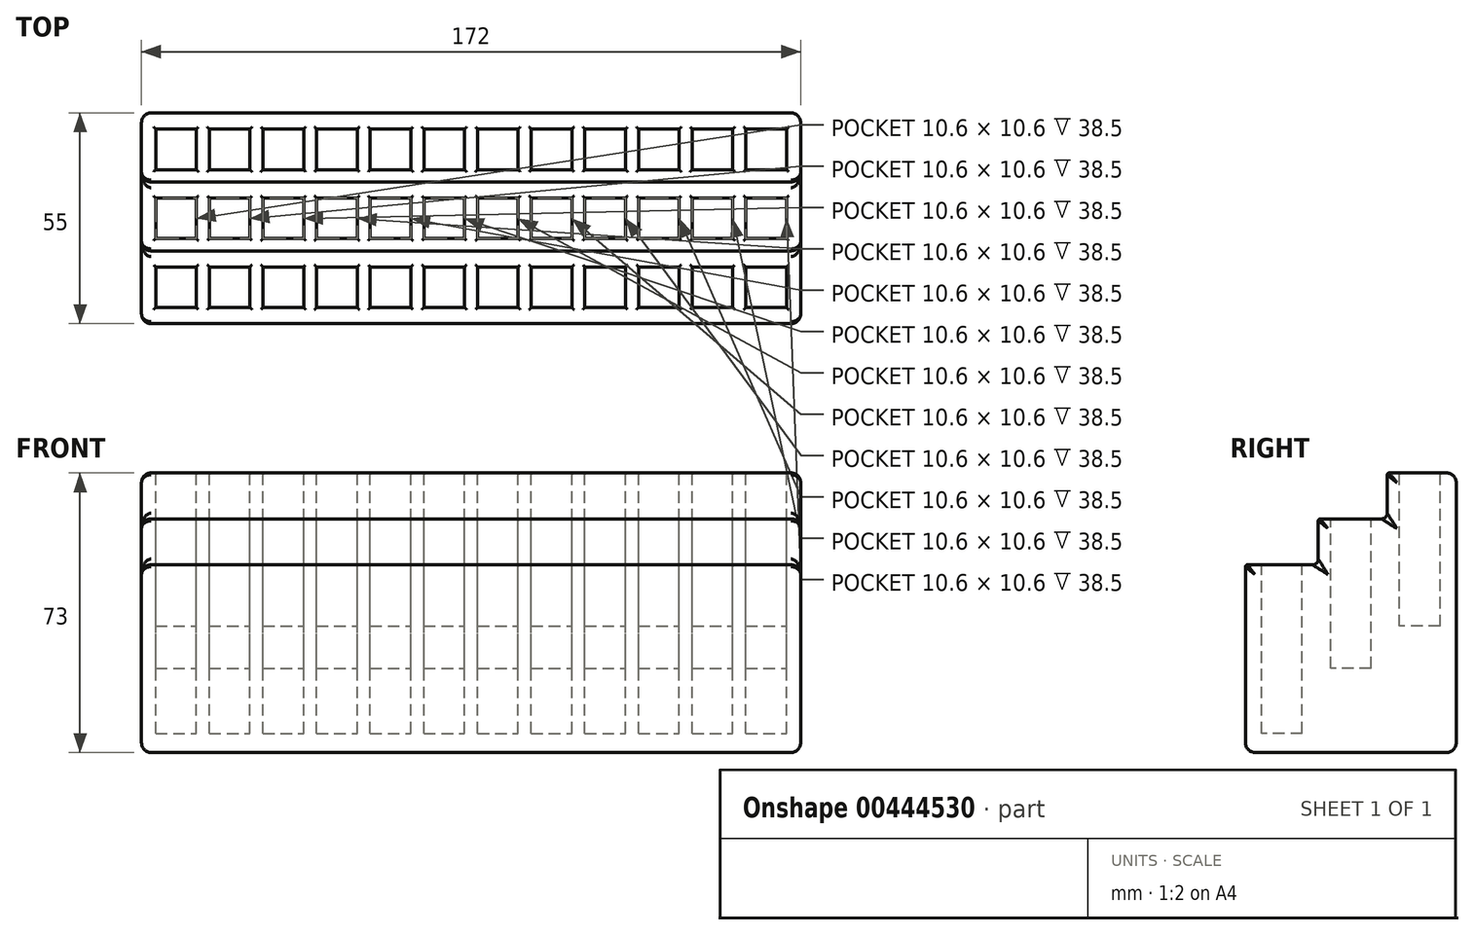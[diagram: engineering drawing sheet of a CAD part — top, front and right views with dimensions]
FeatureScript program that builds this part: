
annotation { "Feature Type Name" : "Feature", "Feature Type Description" : "" }
export const myFeature = defineFeature(function(context is Context, id is Id, definition is map)
    precondition{}
    {
        {
            var Q0;
            Q0=qCreatedBy(makeId("Top.planeOp"),FACE);
            var sketch = newSketch(context, id + "F0", { "sketchPlane" : qUnion([Q0])});
            skLineSegment(sketch, "E0.bottom", {"start": v(-55.78, 92.87) * mm, "end": v(116.22, 92.87) * mm});
            skLineSegment(sketch, "E0.top", {"start": v(-55.78, 37.87) * mm, "end": v(116.22, 37.87) * mm});
            skLineSegment(sketch, "E0.left", {"start": v(-55.78, 92.87) * mm, "end": v(-55.78, 37.87) * mm});
            skLineSegment(sketch, "E0.right", {"start": v(116.22, 92.87) * mm, "end": v(116.22, 37.87) * mm});
            skSolve(sketch);
        }
        {
            var Q0;
            Q0=makeQuery(id+"F0.imprint","IMPRINT",FACE,{"disambiguationData":[TD([[makeQuery(id+"F0.imprint","IMPRINT",EDGE,{"derivedFrom":sQuery(id+"F0.wireOp",EDGE,"2cde3dd9-bf48-4d98-be25-aab0bfc94084.7.2.0")}),-1.0]])]});
            var Q1;
            Q1=makeQuery(id+"F0.imprint","IMPRINT",FACE,{"disambiguationData":[TD([[makeQuery(id+"F0.imprint","IMPRINT",EDGE,{"derivedFrom":sQuery(id+"F0.wireOp",EDGE,"2cde3dd9-bf48-4d98-be25-aab0bfc94084.4.0.0")}),-1.0]])]});
            var Q2;
            Q2=makeQuery(id+"F0.imprint","IMPRINT",FACE,{"disambiguationData":[TD([[makeQuery(id+"F0.imprint","IMPRINT",EDGE,{"derivedFrom":sQuery(id+"F0.wireOp",EDGE,"2cde3dd9-bf48-4d98-be25-aab0bfc94084.3.0.0")}),-1.0]])]});
            var Q3;
            Q3=makeQuery(id+"F0.imprint","IMPRINT",FACE,{"disambiguationData":[TD([[makeQuery(id+"F0.imprint","IMPRINT",EDGE,{"derivedFrom":sQuery(id+"F0.wireOp",EDGE,"2cde3dd9-bf48-4d98-be25-aab0bfc94084.9.2.0")}),-1.0]])]});
            var Q4;
            Q4=makeQuery(id+"F0.imprint","IMPRINT",FACE,{"disambiguationData":[TD([[makeQuery(id+"F0.imprint","IMPRINT",EDGE,{"derivedFrom":sQuery(id+"F0.wireOp",EDGE,"2cde3dd9-bf48-4d98-be25-aab0bfc94084.7.1.0")}),-1.0]])]});
            var Q5;
            Q5=makeQuery(id+"F0.imprint","IMPRINT",FACE,{"disambiguationData":[TD([[makeQuery(id+"F0.imprint","IMPRINT",EDGE,{"derivedFrom":sQuery(id+"F0.wireOp",EDGE,"2cde3dd9-bf48-4d98-be25-aab0bfc94084.0.1.0")}),1.0]])]});
            var Q6;
            Q6=makeQuery(id+"F0.imprint","IMPRINT",FACE,{"disambiguationData":[TD([[makeQuery(id+"F0.imprint","IMPRINT",EDGE,{"derivedFrom":sQuery(id+"F0.wireOp",EDGE,"2cde3dd9-bf48-4d98-be25-aab0bfc94084.8.1.0")}),-1.0]])]});
            var Q7;
            {var subQ0=sQuery(id+"F0.wireOp",EDGE,"E0.top");Q7=makeQuery(id+"F0.imprint","IMPRINT",FACE,{"disambiguationData":[TD([[makeQuery(id+"F0.imprint","IMPRINT",EDGE,{"derivedFrom":subQ0}),1.0]])]});}
            var Q8;
            Q8=makeQuery(id+"F0.imprint","IMPRINT",FACE,{"disambiguationData":[TD([[makeQuery(id+"F0.imprint","IMPRINT",EDGE,{"derivedFrom":sQuery(id+"F0.wireOp",EDGE,"2cde3dd9-bf48-4d98-be25-aab0bfc94084.11.2.0")}),-1.0]])]});
            var Q9;
            Q9=makeQuery(id+"F0.imprint","IMPRINT",FACE,{"disambiguationData":[TD([[makeQuery(id+"F0.imprint","IMPRINT",EDGE,{"derivedFrom":sQuery(id+"F0.wireOp",EDGE,"2cde3dd9-bf48-4d98-be25-aab0bfc94084.5.1.0")}),-1.0]])]});
            var Q10;
            Q10=makeQuery(id+"F0.imprint","IMPRINT",FACE,{"disambiguationData":[TD([[makeQuery(id+"F0.imprint","IMPRINT",EDGE,{"derivedFrom":sQuery(id+"F0.wireOp",EDGE,"2cde3dd9-bf48-4d98-be25-aab0bfc94084.11.1.0")}),-1.0]])]});
            var Q11;
            Q11=makeQuery(id+"F0.imprint","IMPRINT",FACE,{"disambiguationData":[TD([[makeQuery(id+"F0.imprint","IMPRINT",EDGE,{"derivedFrom":sQuery(id+"F0.wireOp",EDGE,"2cde3dd9-bf48-4d98-be25-aab0bfc94084.11.0.0")}),-1.0]])]});
            var Q12;
            Q12=makeQuery(id+"F0.imprint","IMPRINT",FACE,{"disambiguationData":[TD([[makeQuery(id+"F0.imprint","IMPRINT",EDGE,{"derivedFrom":sQuery(id+"F0.wireOp",EDGE,"2cde3dd9-bf48-4d98-be25-aab0bfc94084.5.0.0")}),-1.0]])]});
            var Q13;
            Q13=makeQuery(id+"F0.imprint","IMPRINT",FACE,{"disambiguationData":[TD([[makeQuery(id+"F0.imprint","IMPRINT",EDGE,{"derivedFrom":sQuery(id+"F0.wireOp",EDGE,"2cde3dd9-bf48-4d98-be25-aab0bfc94084.7.0.0")}),-1.0]])]});
            var Q14;
            Q14=makeQuery(id+"F0.imprint","IMPRINT",FACE,{"disambiguationData":[TD([[makeQuery(id+"F0.imprint","IMPRINT",EDGE,{"derivedFrom":sQuery(id+"F0.wireOp",EDGE,"2cde3dd9-bf48-4d98-be25-aab0bfc94084.6.2.0")}),-1.0]])]});
            var Q15;
            {var subQ1=sQuery(id+"F0.wireOp",EDGE,"E0.bottom");Q15=makeQuery(id+"F0.imprint","IMPRINT",FACE,{"disambiguationData":[TD([[makeQuery(id+"F0.imprint","IMPRINT",EDGE,{"derivedFrom":subQ1}),-1.0]])]});}
            var Q16;
            Q16=makeQuery(id+"F0.imprint","IMPRINT",FACE,{"disambiguationData":[TD([[makeQuery(id+"F0.imprint","IMPRINT",EDGE,{"derivedFrom":sQuery(id+"F0.wireOp",EDGE,"2cde3dd9-bf48-4d98-be25-aab0bfc94084.10.0.0")}),-1.0]])]});
            var Q17;
            Q17=makeQuery(id+"F0.imprint","IMPRINT",FACE,{"disambiguationData":[TD([[makeQuery(id+"F0.imprint","IMPRINT",EDGE,{"derivedFrom":sQuery(id+"F0.wireOp",EDGE,"2cde3dd9-bf48-4d98-be25-aab0bfc94084.6.1.0")}),-1.0]])]});
            var Q18;
            Q18=makeQuery(id+"F0.imprint","IMPRINT",FACE,{"disambiguationData":[TD([[makeQuery(id+"F0.imprint","IMPRINT",EDGE,{"derivedFrom":sQuery(id+"F0.wireOp",EDGE,"2cde3dd9-bf48-4d98-be25-aab0bfc94084.6.0.0")}),-1.0]])]});
            var Q19;
            Q19=makeQuery(id+"F0.imprint","IMPRINT",FACE,{"disambiguationData":[TD([[makeQuery(id+"F0.imprint","IMPRINT",EDGE,{"derivedFrom":sQuery(id+"F0.wireOp",EDGE,"2cde3dd9-bf48-4d98-be25-aab0bfc94084.9.1.0")}),-1.0]])]});
            var Q20;
            Q20=makeQuery(id+"F0.imprint","IMPRINT",FACE,{"disambiguationData":[TD([[makeQuery(id+"F0.imprint","IMPRINT",EDGE,{"derivedFrom":sQuery(id+"F0.wireOp",EDGE,"2cde3dd9-bf48-4d98-be25-aab0bfc94084.9.0.0")}),-1.0]])]});
            var Q21;
            Q21=makeQuery(id+"F0.imprint","IMPRINT",FACE,{"disambiguationData":[TD([[makeQuery(id+"F0.imprint","IMPRINT",EDGE,{"derivedFrom":sQuery(id+"F0.wireOp",EDGE,"2cde3dd9-bf48-4d98-be25-aab0bfc94084.8.0.0")}),-1.0]])]});
            var Q22;
            Q22=makeQuery(id+"F0.imprint","IMPRINT",FACE,{"disambiguationData":[TD([[makeQuery(id+"F0.imprint","IMPRINT",EDGE,{"derivedFrom":sQuery(id+"F0.wireOp",EDGE,"2cde3dd9-bf48-4d98-be25-aab0bfc94084.10.1.0")}),-1.0]])]});
            var Q23;
            Q23=makeQuery(id+"F0.imprint","IMPRINT",FACE,{"disambiguationData":[TD([[makeQuery(id+"F0.imprint","IMPRINT",EDGE,{"derivedFrom":sQuery(id+"F0.wireOp",EDGE,"2cde3dd9-bf48-4d98-be25-aab0bfc94084.10.2.0")}),-1.0]])]});
            var Q24;
            Q24=makeQuery(id+"F0.imprint","IMPRINT",FACE,{"disambiguationData":[TD([[makeQuery(id+"F0.imprint","IMPRINT",EDGE,{"derivedFrom":sQuery(id+"F0.wireOp",EDGE,"2cde3dd9-bf48-4d98-be25-aab0bfc94084.8.2.0")}),-1.0]])]});
            var Q25;
            Q25=makeQuery(id+"F0.imprint","IMPRINT",FACE,{"disambiguationData":[TD([[makeQuery(id+"F0.imprint","IMPRINT",EDGE,{"derivedFrom":sQuery(id+"F0.wireOp",EDGE,"2cde3dd9-bf48-4d98-be25-aab0bfc94084.3.2.0")}),-1.0]])]});
            var Q26;
            Q26=makeQuery(id+"F0.imprint","IMPRINT",FACE,{"disambiguationData":[TD([[makeQuery(id+"F0.imprint","IMPRINT",EDGE,{"derivedFrom":sQuery(id+"F0.wireOp",EDGE,"2cde3dd9-bf48-4d98-be25-aab0bfc94084.3.1.0")}),-1.0]])]});
            var Q27;
            Q27=makeQuery(id+"F0.imprint","IMPRINT",FACE,{"disambiguationData":[TD([[makeQuery(id+"F0.imprint","IMPRINT",EDGE,{"derivedFrom":sQuery(id+"F0.wireOp",EDGE,"2cde3dd9-bf48-4d98-be25-aab0bfc94084.2.2.0")}),-1.0]])]});
            var Q28;
            Q28=makeQuery(id+"F0.imprint","IMPRINT",FACE,{"disambiguationData":[TD([[makeQuery(id+"F0.imprint","IMPRINT",EDGE,{"derivedFrom":sQuery(id+"F0.wireOp",EDGE,"2cde3dd9-bf48-4d98-be25-aab0bfc94084.2.1.0")}),-1.0]])]});
            var Q29;
            Q29=makeQuery(id+"F0.imprint","IMPRINT",FACE,{"disambiguationData":[TD([[makeQuery(id+"F0.imprint","IMPRINT",EDGE,{"derivedFrom":sQuery(id+"F0.wireOp",EDGE,"2cde3dd9-bf48-4d98-be25-aab0bfc94084.0.2.0")}),-1.0]])]});
            var Q30;
            Q30=makeQuery(id+"F0.imprint","IMPRINT",FACE,{"disambiguationData":[TD([[makeQuery(id+"F0.imprint","IMPRINT",EDGE,{"derivedFrom":sQuery(id+"F0.wireOp",EDGE,"2cde3dd9-bf48-4d98-be25-aab0bfc94084.2.0.0")}),-1.0]])]});
            var Q31;
            Q31=makeQuery(id+"F0.imprint","IMPRINT",FACE,{"disambiguationData":[TD([[makeQuery(id+"F0.imprint","IMPRINT",EDGE,{"derivedFrom":sQuery(id+"F0.wireOp",EDGE,"2cde3dd9-bf48-4d98-be25-aab0bfc94084.1.2.0")}),-1.0]])]});
            var Q32;
            Q32=makeQuery(id+"F0.imprint","IMPRINT",FACE,{"disambiguationData":[TD([[makeQuery(id+"F0.imprint","IMPRINT",EDGE,{"derivedFrom":sQuery(id+"F0.wireOp",EDGE,"2cde3dd9-bf48-4d98-be25-aab0bfc94084.1.0.0")}),-1.0]])]});
            var Q33;
            Q33=makeQuery(id+"F0.imprint","IMPRINT",FACE,{"disambiguationData":[TD([[makeQuery(id+"F0.imprint","IMPRINT",EDGE,{"derivedFrom":sQuery(id+"F0.wireOp",EDGE,"2cde3dd9-bf48-4d98-be25-aab0bfc94084.0.1.0")}),-1.0]])]});
            var Q34;
            Q34=makeQuery(id+"F0.imprint","IMPRINT",FACE,{"disambiguationData":[TD([[makeQuery(id+"F0.imprint","IMPRINT",EDGE,{"derivedFrom":sQuery(id+"F0.wireOp",EDGE,"2cde3dd9-bf48-4d98-be25-aab0bfc94084.5.2.0")}),-1.0]])]});
            var Q35;
            Q35=makeQuery(id+"F0.imprint","IMPRINT",FACE,{"disambiguationData":[TD([[makeQuery(id+"F0.imprint","IMPRINT",EDGE,{"derivedFrom":sQuery(id+"F0.wireOp",EDGE,"2cde3dd9-bf48-4d98-be25-aab0bfc94084.1.1.0")}),-1.0]])]});
            var Q36;
            Q36=makeQuery(id+"F0.imprint","IMPRINT",FACE,{"disambiguationData":[TD([[makeQuery(id+"F0.imprint","IMPRINT",EDGE,{"derivedFrom":sQuery(id+"F0.wireOp",EDGE,"2cde3dd9-bf48-4d98-be25-aab0bfc94084.4.1.0")}),-1.0]])]});
            var Q37;
            Q37=makeQuery(id+"F0.imprint","IMPRINT",FACE,{"disambiguationData":[TD([[makeQuery(id+"F0.imprint","IMPRINT",EDGE,{"derivedFrom":sQuery(id+"F0.wireOp",EDGE,"2cde3dd9-bf48-4d98-be25-aab0bfc94084.4.2.0")}),-1.0]])]});
            var Q38;
            Q38=makeQuery(id+"F0.imprint","IMPRINT",FACE,{"disambiguationData":[TD([[makeQuery(id+"F0.imprint","IMPRINT",EDGE,{"derivedFrom":sQuery(id+"F0.wireOp",EDGE,"MJ5tnMIe-62KD-FdFw-GlkB-I08ag2kGYmXd.bottom")}),-1.0]])]});
            extrude(context, id + "F1", {"entities" : qUnion([Q0, Q1, Q2, Q3, Q4, Q5, Q6, Q7, Q8, Q9, Q10, Q11, Q12, Q13, Q14, Q15, Q16, Q17, Q18, Q19, Q20, Q21, Q22, Q23, Q24, Q25, Q26, Q27, Q28, Q29, Q30, Q31, Q32, Q33, Q34, Q35, Q36, Q37, Q38]), "oppositeDirection" : true, "depth" : 73 * mm});
        }
        {
            var Q0;
            Q0=makeQuery(id+"F1.opExtrude","CAP_FACE",FACE,{"disambiguationData":[OSD([sQuery(id+"F0.wireOp",EDGE,"E0.bottom"),sQuery(id+"F0.wireOp",EDGE,"E0.top"),sQuery(id+"F0.wireOp",EDGE,"E0.left"),sQuery(id+"F0.wireOp",EDGE,"E0.right")])],"isStart":true});
            var sketch = newSketch(context, id + "F2", { "sketchPlane" : qUnion([Q0])});
            skLineSegment(sketch, "E1.0", {"start": v(-55.78, 37.87) * mm, "end": v(116.22, 37.87) * mm});
            skLineSegment(sketch, "E2.0", {"start": v(116.22, 92.87) * mm, "end": v(116.22, 37.87) * mm});
            skLineSegment(sketch, "E3.0", {"start": v(-55.78, 92.87) * mm, "end": v(116.22, 92.87) * mm});
            skLineSegment(sketch, "E4.0", {"start": v(-55.78, 92.87) * mm, "end": v(-55.78, 37.87) * mm});
            skLineSegment(sketch, "E5.bottom", {"start": v(-52.08, 88.67) * mm, "end": v(-41.48, 88.67) * mm});
            skLineSegment(sketch, "E5.top", {"start": v(-52.08, 78.07) * mm, "end": v(-41.48, 78.07) * mm});
            skLineSegment(sketch, "E5.left", {"start": v(-52.08, 88.67) * mm, "end": v(-52.08, 78.07) * mm});
            skLineSegment(sketch, "E5.right", {"start": v(-41.48, 88.67) * mm, "end": v(-41.48, 78.07) * mm});
            skLineSegment(sketch, "E6.0.1.0", {"start": v(-52.08, 60.07) * mm, "end": v(-41.48, 60.07) * mm});
            skLineSegment(sketch, "E6.0.1.1", {"start": v(-41.48, 70.67) * mm, "end": v(-41.48, 60.07) * mm});
            skLineSegment(sketch, "E6.0.1.2", {"start": v(-52.08, 70.67) * mm, "end": v(-52.08, 60.07) * mm});
            skLineSegment(sketch, "E6.0.1.3", {"start": v(-52.08, 70.67) * mm, "end": v(-41.48, 70.67) * mm});
            skLineSegment(sketch, "E6.0.2.0", {"start": v(-52.08, 42.07) * mm, "end": v(-41.48, 42.07) * mm});
            skLineSegment(sketch, "E6.0.2.1", {"start": v(-41.48, 52.67) * mm, "end": v(-41.48, 42.07) * mm});
            skLineSegment(sketch, "E6.0.2.2", {"start": v(-52.08, 52.67) * mm, "end": v(-52.08, 42.07) * mm});
            skLineSegment(sketch, "E6.0.2.3", {"start": v(-52.08, 52.67) * mm, "end": v(-41.48, 52.67) * mm});
            skLineSegment(sketch, "E6.1.0.0", {"start": v(-38.08, 78.07) * mm, "end": v(-27.48, 78.07) * mm});
            skLineSegment(sketch, "E6.1.0.1", {"start": v(-27.48, 88.67) * mm, "end": v(-27.48, 78.07) * mm});
            skLineSegment(sketch, "E6.1.0.2", {"start": v(-38.08, 88.67) * mm, "end": v(-38.08, 78.07) * mm});
            skLineSegment(sketch, "E6.1.0.3", {"start": v(-38.08, 88.67) * mm, "end": v(-27.48, 88.67) * mm});
            skLineSegment(sketch, "E6.1.1.0", {"start": v(-38.08, 60.07) * mm, "end": v(-27.48, 60.07) * mm});
            skLineSegment(sketch, "E6.1.1.1", {"start": v(-27.48, 70.67) * mm, "end": v(-27.48, 60.07) * mm});
            skLineSegment(sketch, "E6.1.1.2", {"start": v(-38.08, 70.67) * mm, "end": v(-38.08, 60.07) * mm});
            skLineSegment(sketch, "E6.1.1.3", {"start": v(-38.08, 70.67) * mm, "end": v(-27.48, 70.67) * mm});
            skLineSegment(sketch, "E6.1.2.0", {"start": v(-38.08, 42.07) * mm, "end": v(-27.48, 42.07) * mm});
            skLineSegment(sketch, "E6.1.2.1", {"start": v(-27.48, 52.67) * mm, "end": v(-27.48, 42.07) * mm});
            skLineSegment(sketch, "E6.1.2.2", {"start": v(-38.08, 52.67) * mm, "end": v(-38.08, 42.07) * mm});
            skLineSegment(sketch, "E6.1.2.3", {"start": v(-38.08, 52.67) * mm, "end": v(-27.48, 52.67) * mm});
            skLineSegment(sketch, "E6.2.0.0", {"start": v(-24.08, 78.07) * mm, "end": v(-13.48, 78.07) * mm});
            skLineSegment(sketch, "E6.2.0.1", {"start": v(-13.48, 88.67) * mm, "end": v(-13.48, 78.07) * mm});
            skLineSegment(sketch, "E6.2.0.2", {"start": v(-24.08, 88.67) * mm, "end": v(-24.08, 78.07) * mm});
            skLineSegment(sketch, "E6.2.0.3", {"start": v(-24.08, 88.67) * mm, "end": v(-13.48, 88.67) * mm});
            skLineSegment(sketch, "E6.2.1.0", {"start": v(-24.08, 60.07) * mm, "end": v(-13.48, 60.07) * mm});
            skLineSegment(sketch, "E6.2.1.1", {"start": v(-13.48, 70.67) * mm, "end": v(-13.48, 60.07) * mm});
            skLineSegment(sketch, "E6.2.1.2", {"start": v(-24.08, 70.67) * mm, "end": v(-24.08, 60.07) * mm});
            skLineSegment(sketch, "E6.2.1.3", {"start": v(-24.08, 70.67) * mm, "end": v(-13.48, 70.67) * mm});
            skLineSegment(sketch, "E6.2.2.0", {"start": v(-24.08, 42.07) * mm, "end": v(-13.48, 42.07) * mm});
            skLineSegment(sketch, "E6.2.2.1", {"start": v(-13.48, 52.67) * mm, "end": v(-13.48, 42.07) * mm});
            skLineSegment(sketch, "E6.2.2.2", {"start": v(-24.08, 52.67) * mm, "end": v(-24.08, 42.07) * mm});
            skLineSegment(sketch, "E6.2.2.3", {"start": v(-24.08, 52.67) * mm, "end": v(-13.48, 52.67) * mm});
            skLineSegment(sketch, "E6.3.0.0", {"start": v(-10.08, 78.07) * mm, "end": v(0.52, 78.07) * mm});
            skLineSegment(sketch, "E6.3.0.1", {"start": v(0.52, 88.67) * mm, "end": v(0.52, 78.07) * mm});
            skLineSegment(sketch, "E6.3.0.2", {"start": v(-10.08, 88.67) * mm, "end": v(-10.08, 78.07) * mm});
            skLineSegment(sketch, "E6.3.0.3", {"start": v(-10.08, 88.67) * mm, "end": v(0.52, 88.67) * mm});
            skLineSegment(sketch, "E6.3.1.0", {"start": v(-10.08, 60.07) * mm, "end": v(0.52, 60.07) * mm});
            skLineSegment(sketch, "E6.3.1.1", {"start": v(0.52, 70.67) * mm, "end": v(0.52, 60.07) * mm});
            skLineSegment(sketch, "E6.3.1.2", {"start": v(-10.08, 70.67) * mm, "end": v(-10.08, 60.07) * mm});
            skLineSegment(sketch, "E6.3.1.3", {"start": v(-10.08, 70.67) * mm, "end": v(0.52, 70.67) * mm});
            skLineSegment(sketch, "E6.3.2.0", {"start": v(-10.08, 42.07) * mm, "end": v(0.52, 42.07) * mm});
            skLineSegment(sketch, "E6.3.2.1", {"start": v(0.52, 52.67) * mm, "end": v(0.52, 42.07) * mm});
            skLineSegment(sketch, "E6.3.2.2", {"start": v(-10.08, 52.67) * mm, "end": v(-10.08, 42.07) * mm});
            skLineSegment(sketch, "E6.3.2.3", {"start": v(-10.08, 52.67) * mm, "end": v(0.52, 52.67) * mm});
            skLineSegment(sketch, "E6.4.0.0", {"start": v(3.92, 78.07) * mm, "end": v(14.52, 78.07) * mm});
            skLineSegment(sketch, "E6.4.0.1", {"start": v(14.52, 88.67) * mm, "end": v(14.52, 78.07) * mm});
            skLineSegment(sketch, "E6.4.0.2", {"start": v(3.92, 88.67) * mm, "end": v(3.92, 78.07) * mm});
            skLineSegment(sketch, "E6.4.0.3", {"start": v(3.92, 88.67) * mm, "end": v(14.52, 88.67) * mm});
            skLineSegment(sketch, "E6.4.1.0", {"start": v(3.92, 60.07) * mm, "end": v(14.52, 60.07) * mm});
            skLineSegment(sketch, "E6.4.1.1", {"start": v(14.52, 70.67) * mm, "end": v(14.52, 60.07) * mm});
            skLineSegment(sketch, "E6.4.1.2", {"start": v(3.92, 70.67) * mm, "end": v(3.92, 60.07) * mm});
            skLineSegment(sketch, "E6.4.1.3", {"start": v(3.92, 70.67) * mm, "end": v(14.52, 70.67) * mm});
            skLineSegment(sketch, "E6.4.2.0", {"start": v(3.92, 42.07) * mm, "end": v(14.52, 42.07) * mm});
            skLineSegment(sketch, "E6.4.2.1", {"start": v(14.52, 52.67) * mm, "end": v(14.52, 42.07) * mm});
            skLineSegment(sketch, "E6.4.2.2", {"start": v(3.92, 52.67) * mm, "end": v(3.92, 42.07) * mm});
            skLineSegment(sketch, "E6.4.2.3", {"start": v(3.92, 52.67) * mm, "end": v(14.52, 52.67) * mm});
            skLineSegment(sketch, "E6.5.0.0", {"start": v(17.92, 78.07) * mm, "end": v(28.52, 78.07) * mm});
            skLineSegment(sketch, "E6.5.0.1", {"start": v(28.52, 88.67) * mm, "end": v(28.52, 78.07) * mm});
            skLineSegment(sketch, "E6.5.0.2", {"start": v(17.92, 88.67) * mm, "end": v(17.92, 78.07) * mm});
            skLineSegment(sketch, "E6.5.0.3", {"start": v(17.92, 88.67) * mm, "end": v(28.52, 88.67) * mm});
            skLineSegment(sketch, "E6.5.1.0", {"start": v(17.92, 60.07) * mm, "end": v(28.52, 60.07) * mm});
            skLineSegment(sketch, "E6.5.1.1", {"start": v(28.52, 70.67) * mm, "end": v(28.52, 60.07) * mm});
            skLineSegment(sketch, "E6.5.1.2", {"start": v(17.92, 70.67) * mm, "end": v(17.92, 60.07) * mm});
            skLineSegment(sketch, "E6.5.1.3", {"start": v(17.92, 70.67) * mm, "end": v(28.52, 70.67) * mm});
            skLineSegment(sketch, "E6.5.2.0", {"start": v(17.92, 42.07) * mm, "end": v(28.52, 42.07) * mm});
            skLineSegment(sketch, "E6.5.2.1", {"start": v(28.52, 52.67) * mm, "end": v(28.52, 42.07) * mm});
            skLineSegment(sketch, "E6.5.2.2", {"start": v(17.92, 52.67) * mm, "end": v(17.92, 42.07) * mm});
            skLineSegment(sketch, "E6.5.2.3", {"start": v(17.92, 52.67) * mm, "end": v(28.52, 52.67) * mm});
            skLineSegment(sketch, "E6.6.0.0", {"start": v(31.92, 78.07) * mm, "end": v(42.52, 78.07) * mm});
            skLineSegment(sketch, "E6.6.0.1", {"start": v(42.52, 88.67) * mm, "end": v(42.52, 78.07) * mm});
            skLineSegment(sketch, "E6.6.0.2", {"start": v(31.92, 88.67) * mm, "end": v(31.92, 78.07) * mm});
            skLineSegment(sketch, "E6.6.0.3", {"start": v(31.92, 88.67) * mm, "end": v(42.52, 88.67) * mm});
            skLineSegment(sketch, "E6.6.1.0", {"start": v(31.92, 60.07) * mm, "end": v(42.52, 60.07) * mm});
            skLineSegment(sketch, "E6.6.1.1", {"start": v(42.52, 70.67) * mm, "end": v(42.52, 60.07) * mm});
            skLineSegment(sketch, "E6.6.1.2", {"start": v(31.92, 70.67) * mm, "end": v(31.92, 60.07) * mm});
            skLineSegment(sketch, "E6.6.1.3", {"start": v(31.92, 70.67) * mm, "end": v(42.52, 70.67) * mm});
            skLineSegment(sketch, "E6.6.2.0", {"start": v(31.92, 42.07) * mm, "end": v(42.52, 42.07) * mm});
            skLineSegment(sketch, "E6.6.2.1", {"start": v(42.52, 52.67) * mm, "end": v(42.52, 42.07) * mm});
            skLineSegment(sketch, "E6.6.2.2", {"start": v(31.92, 52.67) * mm, "end": v(31.92, 42.07) * mm});
            skLineSegment(sketch, "E6.6.2.3", {"start": v(31.92, 52.67) * mm, "end": v(42.52, 52.67) * mm});
            skLineSegment(sketch, "E6.7.0.0", {"start": v(45.92, 78.07) * mm, "end": v(56.52, 78.07) * mm});
            skLineSegment(sketch, "E6.7.0.1", {"start": v(56.52, 88.67) * mm, "end": v(56.52, 78.07) * mm});
            skLineSegment(sketch, "E6.7.0.2", {"start": v(45.92, 88.67) * mm, "end": v(45.92, 78.07) * mm});
            skLineSegment(sketch, "E6.7.0.3", {"start": v(45.92, 88.67) * mm, "end": v(56.52, 88.67) * mm});
            skLineSegment(sketch, "E6.7.1.0", {"start": v(45.92, 60.07) * mm, "end": v(56.52, 60.07) * mm});
            skLineSegment(sketch, "E6.7.1.1", {"start": v(56.52, 70.67) * mm, "end": v(56.52, 60.07) * mm});
            skLineSegment(sketch, "E6.7.1.2", {"start": v(45.92, 70.67) * mm, "end": v(45.92, 60.07) * mm});
            skLineSegment(sketch, "E6.7.1.3", {"start": v(45.92, 70.67) * mm, "end": v(56.52, 70.67) * mm});
            skLineSegment(sketch, "E6.7.2.0", {"start": v(45.92, 42.07) * mm, "end": v(56.52, 42.07) * mm});
            skLineSegment(sketch, "E6.7.2.1", {"start": v(56.52, 52.67) * mm, "end": v(56.52, 42.07) * mm});
            skLineSegment(sketch, "E6.7.2.2", {"start": v(45.92, 52.67) * mm, "end": v(45.92, 42.07) * mm});
            skLineSegment(sketch, "E6.7.2.3", {"start": v(45.92, 52.67) * mm, "end": v(56.52, 52.67) * mm});
            skLineSegment(sketch, "E6.8.0.0", {"start": v(59.92, 78.07) * mm, "end": v(70.52, 78.07) * mm});
            skLineSegment(sketch, "E6.8.0.1", {"start": v(70.52, 88.67) * mm, "end": v(70.52, 78.07) * mm});
            skLineSegment(sketch, "E6.8.0.2", {"start": v(59.92, 88.67) * mm, "end": v(59.92, 78.07) * mm});
            skLineSegment(sketch, "E6.8.0.3", {"start": v(59.92, 88.67) * mm, "end": v(70.52, 88.67) * mm});
            skLineSegment(sketch, "E6.8.1.0", {"start": v(59.92, 60.07) * mm, "end": v(70.52, 60.07) * mm});
            skLineSegment(sketch, "E6.8.1.1", {"start": v(70.52, 70.67) * mm, "end": v(70.52, 60.07) * mm});
            skLineSegment(sketch, "E6.8.1.2", {"start": v(59.92, 70.67) * mm, "end": v(59.92, 60.07) * mm});
            skLineSegment(sketch, "E6.8.1.3", {"start": v(59.92, 70.67) * mm, "end": v(70.52, 70.67) * mm});
            skLineSegment(sketch, "E6.8.2.0", {"start": v(59.92, 42.07) * mm, "end": v(70.52, 42.07) * mm});
            skLineSegment(sketch, "E6.8.2.1", {"start": v(70.52, 52.67) * mm, "end": v(70.52, 42.07) * mm});
            skLineSegment(sketch, "E6.8.2.2", {"start": v(59.92, 52.67) * mm, "end": v(59.92, 42.07) * mm});
            skLineSegment(sketch, "E6.8.2.3", {"start": v(59.92, 52.67) * mm, "end": v(70.52, 52.67) * mm});
            skLineSegment(sketch, "E6.9.0.0", {"start": v(73.92, 78.07) * mm, "end": v(84.52, 78.07) * mm});
            skLineSegment(sketch, "E6.9.0.1", {"start": v(84.52, 88.67) * mm, "end": v(84.52, 78.07) * mm});
            skLineSegment(sketch, "E6.9.0.2", {"start": v(73.92, 88.67) * mm, "end": v(73.92, 78.07) * mm});
            skLineSegment(sketch, "E6.9.0.3", {"start": v(73.92, 88.67) * mm, "end": v(84.52, 88.67) * mm});
            skLineSegment(sketch, "E6.9.1.0", {"start": v(73.92, 60.07) * mm, "end": v(84.52, 60.07) * mm});
            skLineSegment(sketch, "E6.9.1.1", {"start": v(84.52, 70.67) * mm, "end": v(84.52, 60.07) * mm});
            skLineSegment(sketch, "E6.9.1.2", {"start": v(73.92, 70.67) * mm, "end": v(73.92, 60.07) * mm});
            skLineSegment(sketch, "E6.9.1.3", {"start": v(73.92, 70.67) * mm, "end": v(84.52, 70.67) * mm});
            skLineSegment(sketch, "E6.9.2.0", {"start": v(73.92, 42.07) * mm, "end": v(84.52, 42.07) * mm});
            skLineSegment(sketch, "E6.9.2.1", {"start": v(84.52, 52.67) * mm, "end": v(84.52, 42.07) * mm});
            skLineSegment(sketch, "E6.9.2.2", {"start": v(73.92, 52.67) * mm, "end": v(73.92, 42.07) * mm});
            skLineSegment(sketch, "E6.9.2.3", {"start": v(73.92, 52.67) * mm, "end": v(84.52, 52.67) * mm});
            skLineSegment(sketch, "E6.10.0.0", {"start": v(87.92, 78.07) * mm, "end": v(98.52, 78.07) * mm});
            skLineSegment(sketch, "E6.10.0.1", {"start": v(98.52, 88.67) * mm, "end": v(98.52, 78.07) * mm});
            skLineSegment(sketch, "E6.10.0.2", {"start": v(87.92, 88.67) * mm, "end": v(87.92, 78.07) * mm});
            skLineSegment(sketch, "E6.10.0.3", {"start": v(87.92, 88.67) * mm, "end": v(98.52, 88.67) * mm});
            skLineSegment(sketch, "E6.10.1.0", {"start": v(87.92, 60.07) * mm, "end": v(98.52, 60.07) * mm});
            skLineSegment(sketch, "E6.10.1.1", {"start": v(98.52, 70.67) * mm, "end": v(98.52, 60.07) * mm});
            skLineSegment(sketch, "E6.10.1.2", {"start": v(87.92, 70.67) * mm, "end": v(87.92, 60.07) * mm});
            skLineSegment(sketch, "E6.10.1.3", {"start": v(87.92, 70.67) * mm, "end": v(98.52, 70.67) * mm});
            skLineSegment(sketch, "E6.10.2.0", {"start": v(87.92, 42.07) * mm, "end": v(98.52, 42.07) * mm});
            skLineSegment(sketch, "E6.10.2.1", {"start": v(98.52, 52.67) * mm, "end": v(98.52, 42.07) * mm});
            skLineSegment(sketch, "E6.10.2.2", {"start": v(87.92, 52.67) * mm, "end": v(87.92, 42.07) * mm});
            skLineSegment(sketch, "E6.10.2.3", {"start": v(87.92, 52.67) * mm, "end": v(98.52, 52.67) * mm});
            skLineSegment(sketch, "E6.11.0.0", {"start": v(101.92, 78.07) * mm, "end": v(112.52, 78.07) * mm});
            skLineSegment(sketch, "E6.11.0.1", {"start": v(112.52, 88.67) * mm, "end": v(112.52, 78.07) * mm});
            skLineSegment(sketch, "E6.11.0.2", {"start": v(101.92, 88.67) * mm, "end": v(101.92, 78.07) * mm});
            skLineSegment(sketch, "E6.11.0.3", {"start": v(101.92, 88.67) * mm, "end": v(112.52, 88.67) * mm});
            skLineSegment(sketch, "E6.11.1.0", {"start": v(101.92, 60.07) * mm, "end": v(112.52, 60.07) * mm});
            skLineSegment(sketch, "E6.11.1.1", {"start": v(112.52, 70.67) * mm, "end": v(112.52, 60.07) * mm});
            skLineSegment(sketch, "E6.11.1.2", {"start": v(101.92, 70.67) * mm, "end": v(101.92, 60.07) * mm});
            skLineSegment(sketch, "E6.11.1.3", {"start": v(101.92, 70.67) * mm, "end": v(112.52, 70.67) * mm});
            skLineSegment(sketch, "E6.11.2.0", {"start": v(101.92, 42.07) * mm, "end": v(112.52, 42.07) * mm});
            skLineSegment(sketch, "E6.11.2.1", {"start": v(112.52, 52.67) * mm, "end": v(112.52, 42.07) * mm});
            skLineSegment(sketch, "E6.11.2.2", {"start": v(101.92, 52.67) * mm, "end": v(101.92, 42.07) * mm});
            skLineSegment(sketch, "E6.11.2.3", {"start": v(101.92, 52.67) * mm, "end": v(112.52, 52.67) * mm});
            skLineSegment(sketch, "E6.direction1", {"start": v(-52.08, 78.07) * mm, "end": v(-38.08, 78.07) * mm, "construction": true});
            skLineSegment(sketch, "E6.direction2", {"start": v(-52.08, 78.07) * mm, "end": v(-52.08, 60.07) * mm, "construction": true});
            skLineSegment(sketch, "E7", {"start": v(112.52, 78.07) * mm, "end": v(112.52, 70.67) * mm});
            skLineSegment(sketch, "E8", {"start": v(112.52, 74.37) * mm, "end": v(116.22, 74.37) * mm});
            skLineSegment(sketch, "E9", {"start": v(112.52, 60.07) * mm, "end": v(112.52, 52.67) * mm});
            skLineSegment(sketch, "E10", {"start": v(112.52, 56.37) * mm, "end": v(116.22, 56.37) * mm});
            skSolve(sketch);
        }
        {
            var Q0;
            Q0=makeQuery(id+"F2.imprint","IMPRINT",FACE,{"disambiguationData":[TD([[makeQuery(id+"F2.imprint","IMPRINT",EDGE,{"derivedFrom":sQuery(id+"F2.wireOp",EDGE,"E5.bottom")}),-1.0]])]});
            var Q1;
            Q1=makeQuery(id+"F2.imprint","IMPRINT",FACE,{"disambiguationData":[TD([[makeQuery(id+"F2.imprint","IMPRINT",EDGE,{"derivedFrom":sQuery(id+"F2.wireOp",EDGE,"E6.0.1.0")}),1.0]])]});
            var Q2;
            Q2=makeQuery(id+"F2.imprint","IMPRINT",FACE,{"disambiguationData":[TD([[makeQuery(id+"F2.imprint","IMPRINT",EDGE,{"derivedFrom":sQuery(id+"F2.wireOp",EDGE,"E6.0.2.0")}),1.0]])]});
            var Q3;
            Q3=makeQuery(id+"F2.imprint","IMPRINT",FACE,{"disambiguationData":[TD([[makeQuery(id+"F2.imprint","IMPRINT",EDGE,{"derivedFrom":sQuery(id+"F2.wireOp",EDGE,"E6.1.2.0")}),1.0]])]});
            var Q4;
            Q4=makeQuery(id+"F2.imprint","IMPRINT",FACE,{"disambiguationData":[TD([[makeQuery(id+"F2.imprint","IMPRINT",EDGE,{"derivedFrom":sQuery(id+"F2.wireOp",EDGE,"E6.1.1.0")}),1.0]])]});
            var Q5;
            Q5=makeQuery(id+"F2.imprint","IMPRINT",FACE,{"disambiguationData":[TD([[makeQuery(id+"F2.imprint","IMPRINT",EDGE,{"derivedFrom":sQuery(id+"F2.wireOp",EDGE,"E6.2.0.0")}),1.0]])]});
            var Q6;
            Q6=makeQuery(id+"F2.imprint","IMPRINT",FACE,{"disambiguationData":[TD([[makeQuery(id+"F2.imprint","IMPRINT",EDGE,{"derivedFrom":sQuery(id+"F2.wireOp",EDGE,"E6.2.1.0")}),1.0]])]});
            var Q7;
            Q7=makeQuery(id+"F2.imprint","IMPRINT",FACE,{"disambiguationData":[TD([[makeQuery(id+"F2.imprint","IMPRINT",EDGE,{"derivedFrom":sQuery(id+"F2.wireOp",EDGE,"E6.1.0.0")}),1.0]])]});
            var Q8;
            Q8=makeQuery(id+"F2.imprint","IMPRINT",FACE,{"disambiguationData":[TD([[makeQuery(id+"F2.imprint","IMPRINT",EDGE,{"derivedFrom":sQuery(id+"F2.wireOp",EDGE,"E6.2.2.0")}),1.0]])]});
            var Q9;
            Q9=makeQuery(id+"F2.imprint","IMPRINT",FACE,{"disambiguationData":[TD([[makeQuery(id+"F2.imprint","IMPRINT",EDGE,{"derivedFrom":sQuery(id+"F2.wireOp",EDGE,"E6.3.2.0")}),1.0]])]});
            var Q10;
            Q10=makeQuery(id+"F2.imprint","IMPRINT",FACE,{"disambiguationData":[TD([[makeQuery(id+"F2.imprint","IMPRINT",EDGE,{"derivedFrom":sQuery(id+"F2.wireOp",EDGE,"E6.4.2.0")}),1.0]])]});
            var Q11;
            Q11=makeQuery(id+"F2.imprint","IMPRINT",FACE,{"disambiguationData":[TD([[makeQuery(id+"F2.imprint","IMPRINT",EDGE,{"derivedFrom":sQuery(id+"F2.wireOp",EDGE,"E6.3.1.0")}),1.0]])]});
            var Q12;
            Q12=makeQuery(id+"F2.imprint","IMPRINT",FACE,{"disambiguationData":[TD([[makeQuery(id+"F2.imprint","IMPRINT",EDGE,{"derivedFrom":sQuery(id+"F2.wireOp",EDGE,"E6.4.1.0")}),1.0]])]});
            var Q13;
            Q13=makeQuery(id+"F2.imprint","IMPRINT",FACE,{"disambiguationData":[TD([[makeQuery(id+"F2.imprint","IMPRINT",EDGE,{"derivedFrom":sQuery(id+"F2.wireOp",EDGE,"E6.4.0.0")}),1.0]])]});
            var Q14;
            Q14=makeQuery(id+"F2.imprint","IMPRINT",FACE,{"disambiguationData":[TD([[makeQuery(id+"F2.imprint","IMPRINT",EDGE,{"derivedFrom":sQuery(id+"F2.wireOp",EDGE,"E6.3.0.0")}),1.0]])]});
            var Q15;
            Q15=makeQuery(id+"F2.imprint","IMPRINT",FACE,{"disambiguationData":[TD([[makeQuery(id+"F2.imprint","IMPRINT",EDGE,{"derivedFrom":sQuery(id+"F2.wireOp",EDGE,"E6.5.0.0")}),1.0]])]});
            var Q16;
            Q16=makeQuery(id+"F2.imprint","IMPRINT",FACE,{"disambiguationData":[TD([[makeQuery(id+"F2.imprint","IMPRINT",EDGE,{"derivedFrom":sQuery(id+"F2.wireOp",EDGE,"E6.6.0.0")}),1.0]])]});
            var Q17;
            Q17=makeQuery(id+"F2.imprint","IMPRINT",FACE,{"disambiguationData":[TD([[makeQuery(id+"F2.imprint","IMPRINT",EDGE,{"derivedFrom":sQuery(id+"F2.wireOp",EDGE,"E6.6.1.0")}),1.0]])]});
            var Q18;
            Q18=makeQuery(id+"F2.imprint","IMPRINT",FACE,{"disambiguationData":[TD([[makeQuery(id+"F2.imprint","IMPRINT",EDGE,{"derivedFrom":sQuery(id+"F2.wireOp",EDGE,"E6.5.2.0")}),1.0]])]});
            var Q19;
            Q19=makeQuery(id+"F2.imprint","IMPRINT",FACE,{"disambiguationData":[TD([[makeQuery(id+"F2.imprint","IMPRINT",EDGE,{"derivedFrom":sQuery(id+"F2.wireOp",EDGE,"E6.6.2.0")}),1.0]])]});
            var Q20;
            Q20=makeQuery(id+"F2.imprint","IMPRINT",FACE,{"disambiguationData":[TD([[makeQuery(id+"F2.imprint","IMPRINT",EDGE,{"derivedFrom":sQuery(id+"F2.wireOp",EDGE,"E6.7.2.0")}),1.0]])]});
            var Q21;
            Q21=makeQuery(id+"F2.imprint","IMPRINT",FACE,{"disambiguationData":[TD([[makeQuery(id+"F2.imprint","IMPRINT",EDGE,{"derivedFrom":sQuery(id+"F2.wireOp",EDGE,"E6.7.1.0")}),1.0]])]});
            var Q22;
            Q22=makeQuery(id+"F2.imprint","IMPRINT",FACE,{"disambiguationData":[TD([[makeQuery(id+"F2.imprint","IMPRINT",EDGE,{"derivedFrom":sQuery(id+"F2.wireOp",EDGE,"E6.7.0.0")}),1.0]])]});
            var Q23;
            Q23=makeQuery(id+"F2.imprint","IMPRINT",FACE,{"disambiguationData":[TD([[makeQuery(id+"F2.imprint","IMPRINT",EDGE,{"derivedFrom":sQuery(id+"F2.wireOp",EDGE,"E6.8.0.0")}),1.0]])]});
            var Q24;
            Q24=makeQuery(id+"F2.imprint","IMPRINT",FACE,{"disambiguationData":[TD([[makeQuery(id+"F2.imprint","IMPRINT",EDGE,{"derivedFrom":sQuery(id+"F2.wireOp",EDGE,"E6.8.1.0")}),1.0]])]});
            var Q25;
            Q25=makeQuery(id+"F2.imprint","IMPRINT",FACE,{"disambiguationData":[TD([[makeQuery(id+"F2.imprint","IMPRINT",EDGE,{"derivedFrom":sQuery(id+"F2.wireOp",EDGE,"E6.8.2.0")}),1.0]])]});
            var Q26;
            Q26=makeQuery(id+"F2.imprint","IMPRINT",FACE,{"disambiguationData":[TD([[makeQuery(id+"F2.imprint","IMPRINT",EDGE,{"derivedFrom":sQuery(id+"F2.wireOp",EDGE,"E6.9.2.0")}),1.0]])]});
            var Q27;
            Q27=makeQuery(id+"F2.imprint","IMPRINT",FACE,{"disambiguationData":[TD([[makeQuery(id+"F2.imprint","IMPRINT",EDGE,{"derivedFrom":sQuery(id+"F2.wireOp",EDGE,"E6.9.1.0")}),1.0]])]});
            var Q28;
            Q28=makeQuery(id+"F2.imprint","IMPRINT",FACE,{"disambiguationData":[TD([[makeQuery(id+"F2.imprint","IMPRINT",EDGE,{"derivedFrom":sQuery(id+"F2.wireOp",EDGE,"E6.9.0.0")}),1.0]])]});
            var Q29;
            Q29=makeQuery(id+"F2.imprint","IMPRINT",FACE,{"disambiguationData":[TD([[makeQuery(id+"F2.imprint","IMPRINT",EDGE,{"derivedFrom":sQuery(id+"F2.wireOp",EDGE,"E6.10.0.0")}),1.0]])]});
            var Q30;
            Q30=makeQuery(id+"F2.imprint","IMPRINT",FACE,{"disambiguationData":[TD([[makeQuery(id+"F2.imprint","IMPRINT",EDGE,{"derivedFrom":sQuery(id+"F2.wireOp",EDGE,"E6.10.1.0")}),1.0]])]});
            var Q31;
            Q31=makeQuery(id+"F2.imprint","IMPRINT",FACE,{"disambiguationData":[TD([[makeQuery(id+"F2.imprint","IMPRINT",EDGE,{"derivedFrom":sQuery(id+"F2.wireOp",EDGE,"E6.10.2.0")}),1.0]])]});
            var Q32;
            Q32=makeQuery(id+"F2.imprint","IMPRINT",FACE,{"disambiguationData":[TD([[makeQuery(id+"F2.imprint","IMPRINT",EDGE,{"derivedFrom":sQuery(id+"F2.wireOp",EDGE,"E6.11.2.0")}),1.0]])]});
            var Q33;
            Q33=makeQuery(id+"F2.imprint","IMPRINT",FACE,{"disambiguationData":[TD([[makeQuery(id+"F2.imprint","IMPRINT",EDGE,{"derivedFrom":sQuery(id+"F2.wireOp",EDGE,"E6.11.1.0")}),1.0]])]});
            var Q34;
            Q34=makeQuery(id+"F2.imprint","IMPRINT",FACE,{"disambiguationData":[TD([[makeQuery(id+"F2.imprint","IMPRINT",EDGE,{"derivedFrom":sQuery(id+"F2.wireOp",EDGE,"E6.11.0.0")}),1.0]])]});
            var Q35;
            Q35=makeQuery(id+"F2.imprint","IMPRINT",FACE,{"disambiguationData":[TD([[makeQuery(id+"F2.imprint","IMPRINT",EDGE,{"derivedFrom":sQuery(id+"F2.wireOp",EDGE,"E6.5.1.0")}),1.0]])]});
            extrude(context, id + "F3", {"entities" : qUnion([Q0, Q1, Q2, Q3, Q4, Q5, Q6, Q7, Q8, Q9, Q10, Q11, Q12, Q13, Q14, Q15, Q16, Q17, Q18, Q19, Q20, Q21, Q22, Q23, Q24, Q25, Q26, Q27, Q28, Q29, Q30, Q31, Q32, Q33, Q34, Q35]), "operationType" : NewBodyOperationType.REMOVE, "oppositeDirection" : true, "depth" : 68 * mm});
        }
        {
            var Q0;
            Q0=makeQuery(id+"F1.opExtrude","SWEPT_FACE",FACE,{"disambiguationData":[OSD([sQuery(id+"F0.wireOp",EDGE,"E0.right")])]});
            var sketch = newSketch(context, id + "F4", { "sketchPlane" : qUnion([Q0])});
            skLineSegment(sketch, "E11.0", {"start": v(37.87, -73) * mm, "end": v(37.87, 0) * mm});
            skLineSegment(sketch, "E12.0", {"start": v(92.87, -73) * mm, "end": v(92.87, 0) * mm});
            skLineSegment(sketch, "E13.0", {"start": v(92.87, 0) * mm, "end": v(37.87, 0) * mm});
            skLineSegment(sketch, "E14.0", {"start": v(92.87, -73) * mm, "end": v(37.87, -73) * mm});
            skLineSegment(sketch, "E15.0", {"start": v(74.87, -73) * mm, "end": v(74.87, 0) * mm});
            skLineSegment(sketch, "E16.0", {"start": v(56.87, -73) * mm, "end": v(56.87, 0) * mm});
            skLineSegment(sketch, "E17.0", {"start": v(92.87, -12) * mm, "end": v(37.87, -12) * mm});
            skLineSegment(sketch, "E18.0", {"start": v(92.87, -24) * mm, "end": v(37.87, -24) * mm});
            skSolve(sketch);
        }
        {
            var Q0;
            {var subQ0=sQuery(id+"F4.wireOp",EDGE,"E13.0");var subQ1=sQuery(id+"F4.wireOp",EDGE,"E11.0");var subQ2=makeQuery(id+"F4.imprint","INTERSECT",VERTEX,{"derivedFrom":[subQ1,subQ0]});Q0=makeQuery(id+"F4.imprint","IMPRINT",FACE,{"disambiguationData":[TD([[makeQuery(id+"F4.imprint","IMPRINT",EDGE,{"disambiguationData":[TD([[subQ2,1.0]])],"derivedFrom":subQ1}),-1.0]])]});}
            var Q1;
            {var subQ0=sQuery(id+"F4.wireOp",EDGE,"E15.0");var subQ1=sQuery(id+"F4.wireOp",EDGE,"E13.0");var subQ2=makeQuery(id+"F4.imprint","INTERSECT",VERTEX,{"derivedFrom":[subQ1,subQ0]});Q1=makeQuery(id+"F4.imprint","IMPRINT",FACE,{"disambiguationData":[TD([[makeQuery(id+"F4.imprint","IMPRINT",EDGE,{"disambiguationData":[TD([[subQ2,-1.0]])],"derivedFrom":subQ1}),1.0]])]});}
            var Q2;
            {var subQ0=sQuery(id+"F4.wireOp",EDGE,"E17.0");var subQ1=sQuery(id+"F4.wireOp",EDGE,"E11.0");var subQ2=makeQuery(id+"F4.imprint","INTERSECT",VERTEX,{"derivedFrom":[subQ1,subQ0]});Q2=makeQuery(id+"F4.imprint","IMPRINT",FACE,{"disambiguationData":[TD([[makeQuery(id+"F4.imprint","IMPRINT",EDGE,{"disambiguationData":[TD([[subQ2,1.0]])],"derivedFrom":subQ1}),-1.0]])]});}
            extrude(context, id + "F5", {"entities" : qUnion([Q0, Q1, Q2]), "operationType" : NewBodyOperationType.REMOVE, "endBound" : BoundingType.THROUGH_ALL, "oppositeDirection" : true, "depth" : 25 * mm});
        }
        {
            var Q0;
            Q0=makeQuery(id+"F3.boolean.opBoolean","COPY",FACE,{"derivedFrom":makeQuery(id+"F3.opExtrude","CAP_FACE",FACE,{"disambiguationData":[OSD([sQuery(id+"F2.wireOp",EDGE,"E6.11.0.0"),sQuery(id+"F2.wireOp",EDGE,"E6.11.0.1"),sQuery(id+"F2.wireOp",EDGE,"E6.11.0.2"),sQuery(id+"F2.wireOp",EDGE,"E6.11.0.3")])],"isStart":false})});
            var Q1;
            Q1=makeQuery(id+"F3.boolean.opBoolean","COPY",FACE,{"derivedFrom":makeQuery(id+"F3.opExtrude","CAP_FACE",FACE,{"disambiguationData":[OSD([sQuery(id+"F2.wireOp",EDGE,"E6.10.0.0"),sQuery(id+"F2.wireOp",EDGE,"E6.10.0.1"),sQuery(id+"F2.wireOp",EDGE,"E6.10.0.2"),sQuery(id+"F2.wireOp",EDGE,"E6.10.0.3")])],"isStart":false})});
            var Q2;
            Q2=makeQuery(id+"F3.boolean.opBoolean","COPY",FACE,{"derivedFrom":makeQuery(id+"F3.opExtrude","CAP_FACE",FACE,{"disambiguationData":[OSD([sQuery(id+"F2.wireOp",EDGE,"E6.9.0.0"),sQuery(id+"F2.wireOp",EDGE,"E6.9.0.1"),sQuery(id+"F2.wireOp",EDGE,"E6.9.0.2"),sQuery(id+"F2.wireOp",EDGE,"E6.9.0.3")])],"isStart":false})});
            var Q3;
            Q3=makeQuery(id+"F3.boolean.opBoolean","COPY",FACE,{"derivedFrom":makeQuery(id+"F3.opExtrude","CAP_FACE",FACE,{"disambiguationData":[OSD([sQuery(id+"F2.wireOp",EDGE,"E6.8.0.0"),sQuery(id+"F2.wireOp",EDGE,"E6.8.0.1"),sQuery(id+"F2.wireOp",EDGE,"E6.8.0.2"),sQuery(id+"F2.wireOp",EDGE,"E6.8.0.3")])],"isStart":false})});
            var Q4;
            Q4=makeQuery(id+"F3.boolean.opBoolean","COPY",FACE,{"derivedFrom":makeQuery(id+"F3.opExtrude","CAP_FACE",FACE,{"disambiguationData":[OSD([sQuery(id+"F2.wireOp",EDGE,"E6.7.0.0"),sQuery(id+"F2.wireOp",EDGE,"E6.7.0.1"),sQuery(id+"F2.wireOp",EDGE,"E6.7.0.2"),sQuery(id+"F2.wireOp",EDGE,"E6.7.0.3")])],"isStart":false})});
            var Q5;
            Q5=makeQuery(id+"F3.boolean.opBoolean","COPY",FACE,{"derivedFrom":makeQuery(id+"F3.opExtrude","CAP_FACE",FACE,{"disambiguationData":[OSD([sQuery(id+"F2.wireOp",EDGE,"E6.6.0.0"),sQuery(id+"F2.wireOp",EDGE,"E6.6.0.1"),sQuery(id+"F2.wireOp",EDGE,"E6.6.0.2"),sQuery(id+"F2.wireOp",EDGE,"E6.6.0.3")])],"isStart":false})});
            var Q6;
            Q6=makeQuery(id+"F3.boolean.opBoolean","COPY",FACE,{"derivedFrom":makeQuery(id+"F3.opExtrude","CAP_FACE",FACE,{"disambiguationData":[OSD([sQuery(id+"F2.wireOp",EDGE,"E6.5.0.0"),sQuery(id+"F2.wireOp",EDGE,"E6.5.0.1"),sQuery(id+"F2.wireOp",EDGE,"E6.5.0.2"),sQuery(id+"F2.wireOp",EDGE,"E6.5.0.3")])],"isStart":false})});
            var Q7;
            Q7=makeQuery(id+"F3.boolean.opBoolean","COPY",FACE,{"derivedFrom":makeQuery(id+"F3.opExtrude","CAP_FACE",FACE,{"disambiguationData":[OSD([sQuery(id+"F2.wireOp",EDGE,"E6.4.0.0"),sQuery(id+"F2.wireOp",EDGE,"E6.4.0.1"),sQuery(id+"F2.wireOp",EDGE,"E6.4.0.2"),sQuery(id+"F2.wireOp",EDGE,"E6.4.0.3")])],"isStart":false})});
            var Q8;
            Q8=makeQuery(id+"F3.boolean.opBoolean","COPY",FACE,{"derivedFrom":makeQuery(id+"F3.opExtrude","CAP_FACE",FACE,{"disambiguationData":[OSD([sQuery(id+"F2.wireOp",EDGE,"E6.3.0.0"),sQuery(id+"F2.wireOp",EDGE,"E6.3.0.1"),sQuery(id+"F2.wireOp",EDGE,"E6.3.0.2"),sQuery(id+"F2.wireOp",EDGE,"E6.3.0.3")])],"isStart":false})});
            var Q9;
            Q9=makeQuery(id+"F3.boolean.opBoolean","COPY",FACE,{"derivedFrom":makeQuery(id+"F3.opExtrude","CAP_FACE",FACE,{"disambiguationData":[OSD([sQuery(id+"F2.wireOp",EDGE,"E6.2.0.0"),sQuery(id+"F2.wireOp",EDGE,"E6.2.0.1"),sQuery(id+"F2.wireOp",EDGE,"E6.2.0.2"),sQuery(id+"F2.wireOp",EDGE,"E6.2.0.3")])],"isStart":false})});
            var Q10;
            Q10=makeQuery(id+"F3.boolean.opBoolean","COPY",FACE,{"derivedFrom":makeQuery(id+"F3.opExtrude","CAP_FACE",FACE,{"disambiguationData":[OSD([sQuery(id+"F2.wireOp",EDGE,"E6.1.0.0"),sQuery(id+"F2.wireOp",EDGE,"E6.1.0.1"),sQuery(id+"F2.wireOp",EDGE,"E6.1.0.2"),sQuery(id+"F2.wireOp",EDGE,"E6.1.0.3")])],"isStart":false})});
            var Q11;
            Q11=makeQuery(id+"F3.boolean.opBoolean","COPY",FACE,{"derivedFrom":makeQuery(id+"F3.opExtrude","CAP_FACE",FACE,{"disambiguationData":[OSD([sQuery(id+"F2.wireOp",EDGE,"E5.bottom"),sQuery(id+"F2.wireOp",EDGE,"E5.top"),sQuery(id+"F2.wireOp",EDGE,"E5.left"),sQuery(id+"F2.wireOp",EDGE,"E5.right")])],"isStart":false})});
            extrude(context, id + "F6", {"entities" : qUnion([Q0, Q1, Q2, Q3, Q4, Q5, Q6, Q7, Q8, Q9, Q10, Q11]), "operationType" : NewBodyOperationType.ADD, "depth" : 28 * mm});
        }
        {
            var Q0;
            Q0=makeQuery(id+"F3.boolean.opBoolean","COPY",FACE,{"derivedFrom":makeQuery(id+"F3.opExtrude","CAP_FACE",FACE,{"disambiguationData":[OSD([sQuery(id+"F2.wireOp",EDGE,"E6.11.1.0"),sQuery(id+"F2.wireOp",EDGE,"E6.11.1.1"),sQuery(id+"F2.wireOp",EDGE,"E6.11.1.2"),sQuery(id+"F2.wireOp",EDGE,"E6.11.1.3")])],"isStart":false})});
            var Q1;
            Q1=makeQuery(id+"F3.boolean.opBoolean","COPY",FACE,{"derivedFrom":makeQuery(id+"F3.opExtrude","CAP_FACE",FACE,{"disambiguationData":[OSD([sQuery(id+"F2.wireOp",EDGE,"E6.10.1.0"),sQuery(id+"F2.wireOp",EDGE,"E6.10.1.1"),sQuery(id+"F2.wireOp",EDGE,"E6.10.1.2"),sQuery(id+"F2.wireOp",EDGE,"E6.10.1.3")])],"isStart":false})});
            var Q2;
            Q2=makeQuery(id+"F3.boolean.opBoolean","COPY",FACE,{"derivedFrom":makeQuery(id+"F3.opExtrude","CAP_FACE",FACE,{"disambiguationData":[OSD([sQuery(id+"F2.wireOp",EDGE,"E6.9.1.0"),sQuery(id+"F2.wireOp",EDGE,"E6.9.1.1"),sQuery(id+"F2.wireOp",EDGE,"E6.9.1.2"),sQuery(id+"F2.wireOp",EDGE,"E6.9.1.3")])],"isStart":false})});
            var Q3;
            Q3=makeQuery(id+"F3.boolean.opBoolean","COPY",FACE,{"derivedFrom":makeQuery(id+"F3.opExtrude","CAP_FACE",FACE,{"disambiguationData":[OSD([sQuery(id+"F2.wireOp",EDGE,"E6.8.1.0"),sQuery(id+"F2.wireOp",EDGE,"E6.8.1.1"),sQuery(id+"F2.wireOp",EDGE,"E6.8.1.2"),sQuery(id+"F2.wireOp",EDGE,"E6.8.1.3")])],"isStart":false})});
            var Q4;
            Q4=makeQuery(id+"F3.boolean.opBoolean","COPY",FACE,{"derivedFrom":makeQuery(id+"F3.opExtrude","CAP_FACE",FACE,{"disambiguationData":[OSD([sQuery(id+"F2.wireOp",EDGE,"E6.7.1.0"),sQuery(id+"F2.wireOp",EDGE,"E6.7.1.1"),sQuery(id+"F2.wireOp",EDGE,"E6.7.1.2"),sQuery(id+"F2.wireOp",EDGE,"E6.7.1.3")])],"isStart":false})});
            var Q5;
            Q5=makeQuery(id+"F3.boolean.opBoolean","COPY",FACE,{"derivedFrom":makeQuery(id+"F3.opExtrude","CAP_FACE",FACE,{"disambiguationData":[OSD([sQuery(id+"F2.wireOp",EDGE,"E6.6.1.0"),sQuery(id+"F2.wireOp",EDGE,"E6.6.1.1"),sQuery(id+"F2.wireOp",EDGE,"E6.6.1.2"),sQuery(id+"F2.wireOp",EDGE,"E6.6.1.3")])],"isStart":false})});
            var Q6;
            Q6=makeQuery(id+"F3.boolean.opBoolean","COPY",FACE,{"derivedFrom":makeQuery(id+"F3.opExtrude","CAP_FACE",FACE,{"disambiguationData":[OSD([sQuery(id+"F2.wireOp",EDGE,"E6.5.1.0"),sQuery(id+"F2.wireOp",EDGE,"E6.5.1.1"),sQuery(id+"F2.wireOp",EDGE,"E6.5.1.2"),sQuery(id+"F2.wireOp",EDGE,"E6.5.1.3")])],"isStart":false})});
            var Q7;
            Q7=makeQuery(id+"F3.boolean.opBoolean","COPY",FACE,{"derivedFrom":makeQuery(id+"F3.opExtrude","CAP_FACE",FACE,{"disambiguationData":[OSD([sQuery(id+"F2.wireOp",EDGE,"E6.4.1.0"),sQuery(id+"F2.wireOp",EDGE,"E6.4.1.1"),sQuery(id+"F2.wireOp",EDGE,"E6.4.1.2"),sQuery(id+"F2.wireOp",EDGE,"E6.4.1.3")])],"isStart":false})});
            var Q8;
            Q8=makeQuery(id+"F3.boolean.opBoolean","COPY",FACE,{"derivedFrom":makeQuery(id+"F3.opExtrude","CAP_FACE",FACE,{"disambiguationData":[OSD([sQuery(id+"F2.wireOp",EDGE,"E6.3.1.0"),sQuery(id+"F2.wireOp",EDGE,"E6.3.1.1"),sQuery(id+"F2.wireOp",EDGE,"E6.3.1.2"),sQuery(id+"F2.wireOp",EDGE,"E6.3.1.3")])],"isStart":false})});
            var Q9;
            Q9=makeQuery(id+"F3.boolean.opBoolean","COPY",FACE,{"derivedFrom":makeQuery(id+"F3.opExtrude","CAP_FACE",FACE,{"disambiguationData":[OSD([sQuery(id+"F2.wireOp",EDGE,"E6.2.1.0"),sQuery(id+"F2.wireOp",EDGE,"E6.2.1.1"),sQuery(id+"F2.wireOp",EDGE,"E6.2.1.2"),sQuery(id+"F2.wireOp",EDGE,"E6.2.1.3")])],"isStart":false})});
            var Q10;
            Q10=makeQuery(id+"F3.boolean.opBoolean","COPY",FACE,{"derivedFrom":makeQuery(id+"F3.opExtrude","CAP_FACE",FACE,{"disambiguationData":[OSD([sQuery(id+"F2.wireOp",EDGE,"E6.1.1.0"),sQuery(id+"F2.wireOp",EDGE,"E6.1.1.1"),sQuery(id+"F2.wireOp",EDGE,"E6.1.1.2"),sQuery(id+"F2.wireOp",EDGE,"E6.1.1.3")])],"isStart":false})});
            var Q11;
            Q11=makeQuery(id+"F3.boolean.opBoolean","COPY",FACE,{"derivedFrom":makeQuery(id+"F3.opExtrude","CAP_FACE",FACE,{"disambiguationData":[OSD([sQuery(id+"F2.wireOp",EDGE,"E6.0.1.0"),sQuery(id+"F2.wireOp",EDGE,"E6.0.1.1"),sQuery(id+"F2.wireOp",EDGE,"E6.0.1.2"),sQuery(id+"F2.wireOp",EDGE,"E6.0.1.3")])],"isStart":false})});
            extrude(context, id + "F7", {"entities" : qUnion([Q0, Q1, Q2, Q3, Q4, Q5, Q6, Q7, Q8, Q9, Q10, Q11]), "operationType" : NewBodyOperationType.ADD, "depth" : 17 * mm});
        }
        {
            var Q0;
            Q0=makeQuery(id+"F1.opExtrude","CAP_FACE",FACE,{"disambiguationData":[OSD([sQuery(id+"F0.wireOp",EDGE,"E0.bottom"),sQuery(id+"F0.wireOp",EDGE,"E0.top"),sQuery(id+"F0.wireOp",EDGE,"E0.left"),sQuery(id+"F0.wireOp",EDGE,"E0.right")])],"isStart":false});
            var Q1;
            Q1=makeQuery(id+"F1.opExtrude","SWEPT_FACE",FACE,{"disambiguationData":[OSD([sQuery(id+"F0.wireOp",EDGE,"E0.right")])]});
            var Q2;
            Q2=makeQuery(id+"F1.opExtrude","SWEPT_FACE",FACE,{"disambiguationData":[OSD([sQuery(id+"F0.wireOp",EDGE,"E0.left")])]});
            var Q3;
            Q3=makeQuery(id+"F1.opExtrude","SWEPT_FACE",FACE,{"disambiguationData":[OSD([sQuery(id+"F0.wireOp",EDGE,"E0.bottom")])]});
            fillet(context, id + "F8", {"entities" : qUnion([Q0, Q1, Q2, Q3]), "radius" : 2.5 * mm, "tangentPropagation" : true, "allowEdgeOverflow" : false});
        }
        {
            var Q0;
            Q0=makeQuery(id+"F5.boolean.opBoolean","COPY",EDGE,{"derivedFrom":makeQuery(id+"F5.opExtrude","SWEPT_EDGE",EDGE,{"disambiguationData":[OSD([sQuery(id+"F4.wireOp",EDGE,"E15.0"),sQuery(id+"F4.wireOp",EDGE,"E17.0")])]})});
            var Q1;
            Q1=makeQuery(id+"F5.boolean.opBoolean","COPY",EDGE,{"derivedFrom":makeQuery(id+"F5.opExtrude","SWEPT_EDGE",EDGE,{"disambiguationData":[OSD([sQuery(id+"F4.wireOp",EDGE,"E16.0"),sQuery(id+"F4.wireOp",EDGE,"E18.0")])]})});
            fillet(context, id + "F9", {"entities" : qUnion([Q0, Q1]), "radius" : 1.5 * mm, "tangentPropagation" : true, "allowEdgeOverflow" : false});
        }
        {
            var Q0;
            Q0=makeQuery(id+"F1.opExtrude","CAP_FACE",FACE,{"disambiguationData":[OSD([sQuery(id+"F0.wireOp",EDGE,"E0.bottom"),sQuery(id+"F0.wireOp",EDGE,"E0.top"),sQuery(id+"F0.wireOp",EDGE,"E0.left"),sQuery(id+"F0.wireOp",EDGE,"E0.right")])],"isStart":true});
            var Q1;
            Q1=makeQuery(id+"F5.boolean.opBoolean","COPY",FACE,{"derivedFrom":makeQuery(id+"F5.opExtrude","SWEPT_FACE",FACE,{"disambiguationData":[OSD([sQuery(id+"F4.wireOp",EDGE,"E17.0")])]})});
            var Q2;
            Q2=makeQuery(id+"F5.boolean.opBoolean","COPY",FACE,{"derivedFrom":makeQuery(id+"F5.opExtrude","SWEPT_FACE",FACE,{"disambiguationData":[OSD([sQuery(id+"F4.wireOp",EDGE,"E18.0")])]})});
            fillet(context, id + "F10", {"entities" : qUnion([Q0, Q1, Q2]), "radius" : .5 * mm, "tangentPropagation" : true, "allowEdgeOverflow" : false});
        }
    });
